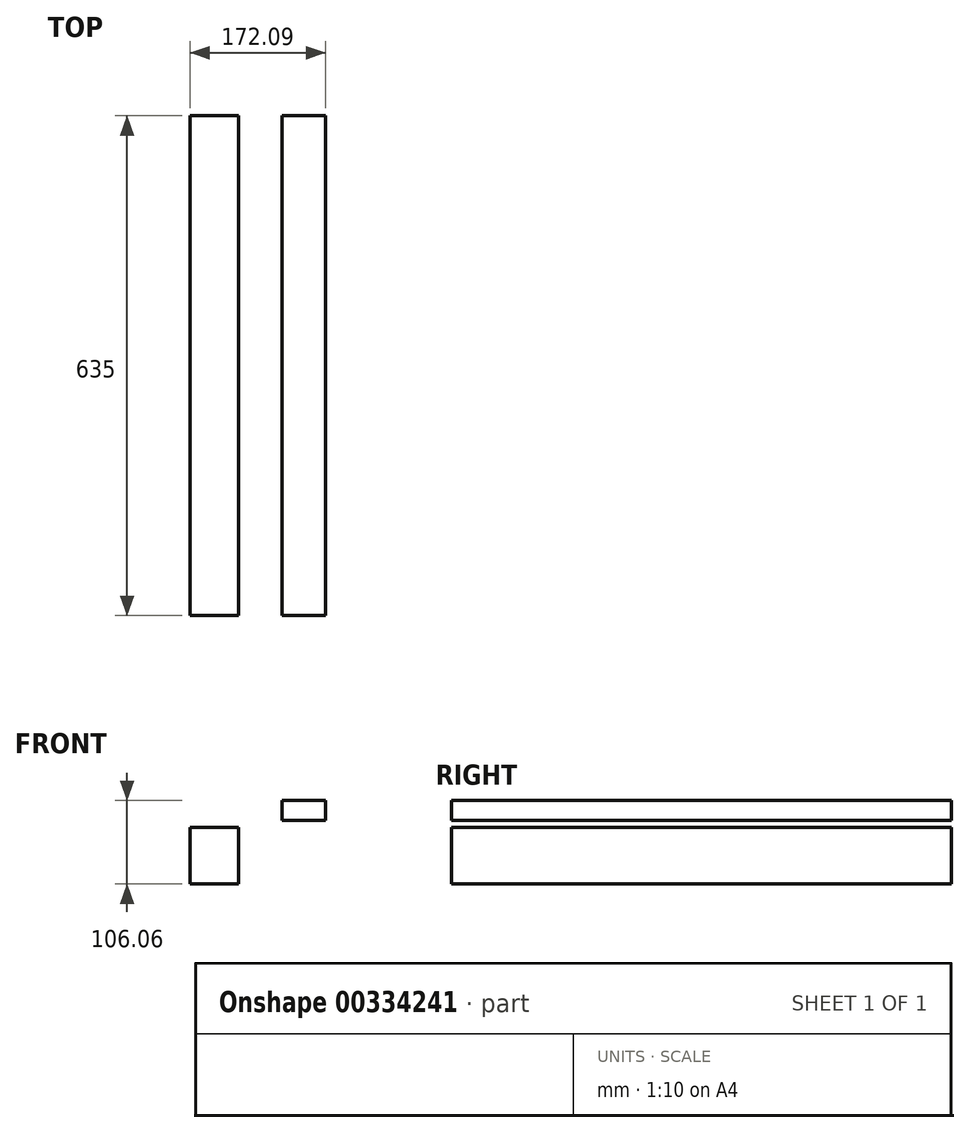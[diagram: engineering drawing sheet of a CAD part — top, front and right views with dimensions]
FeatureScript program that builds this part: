
annotation { "Feature Type Name" : "Feature", "Feature Type Description" : "" }
export const myFeature = defineFeature(function(context is Context, id is Id, definition is map)
    precondition{}
    {
        {
            var Q0;
            Q0=qCreatedBy(makeId("Front.planeOp"),FACE);
            var sketch = newSketch(context, id + "F0", { "sketchPlane" : qUnion([Q0])});
            skLineSegment(sketch, "E0.bottom", {"start": v(30.82, -36.01) * mm, "end": v(-30.82, -36.01) * mm});
            skLineSegment(sketch, "E0.top", {"start": v(30.82, 36.01) * mm, "end": v(-30.82, 36.01) * mm});
            skLineSegment(sketch, "E0.left", {"start": v(30.82, -36.01) * mm, "end": v(30.82, 36.01) * mm});
            skLineSegment(sketch, "E0.right", {"start": v(-30.82, -36.01) * mm, "end": v(-30.82, 36.01) * mm});
            skPoint(sketch, "E0.middle", {"position": v(0, 0) * mm});
            skLineSegment(sketch, "E1.bottom", {"start": v(141.27, 45.1) * mm, "end": v(86.1, 45.1) * mm});
            skLineSegment(sketch, "E1.top", {"start": v(141.27, 70.05) * mm, "end": v(86.1, 70.05) * mm});
            skLineSegment(sketch, "E1.left", {"start": v(141.27, 45.1) * mm, "end": v(141.27, 70.05) * mm});
            skLineSegment(sketch, "E1.right", {"start": v(86.1, 45.1) * mm, "end": v(86.1, 70.05) * mm});
            skPoint(sketch, "E1.middle", {"position": v(113.68, 57.58) * mm});
            skLineSegment(sketch, "E2", {"start": v(30.82, 36.01) * mm, "end": v(30.82, 53.2) * mm});
            skArc(sketch, "E3", {"start": v(30.82, 53.2) * mm, "mid": v(49.22, 71.6) * mm, "end": v(67.62, 53.2) * mm});
            skLineSegment(sketch, "E4", {"start": v(67.62, 53.2) * mm, "end": v(113.26, 53.2) * mm});
            skSolve(sketch);
        }
        {
            var Q0;
            {var subQ0=sQuery(id+"F0.wireOp",EDGE,"E1.bottom");Q0=makeQuery(id+"F0.imprint","IMPRINT",FACE,{"disambiguationData":[TD([[makeQuery(id+"F0.imprint","IMPRINT",EDGE,{"derivedFrom":subQ0}),-1.0]])]});}
            var Q1;
            Q1=makeQuery(id+"F0.imprint","IMPRINT",FACE,{"disambiguationData":[TD([[makeQuery(id+"F0.imprint","IMPRINT",EDGE,{"derivedFrom":sQuery(id+"F0.wireOp",EDGE,"E0.bottom")}),-1.0]])]});
            extrude(context, id + "F1", {"entities" : qUnion([Q0, Q1]), "depth" : 635 * mm});
        }
    });
